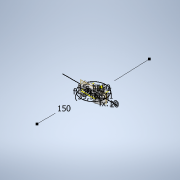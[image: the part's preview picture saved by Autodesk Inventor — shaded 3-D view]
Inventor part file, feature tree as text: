
AUTODESK INVENTOR PART (.ipt)
format: ipt  version: 2020.3 (Build 243373000, 373)  size: 541,184 bytes
history: native  units: mm
features: extrude x9, sketch x9, fillet x2, plane x1, loft x1, mirror x1
ambient origin geometry x8: Origin, YZ Plane, XZ Plane, XY Plane, X Axis, Y Axis, Z Axis, Center Point
bodies: Volumenkörper1 (feature_tree)
feature tree (23):
  extrude  "Extrusion1"  Depth=24.5mm
  extrude  "Extrusion2"  Depth=3.6mm
  extrude  "Extrusion3"  Depth=19.75mm
  extrude  "Extrusion4"  Depth=12.25mm
  sketch  "Skizze5"  dims[d8=0.0mm d9=4.0mm]
  extrude  "Extrusion5"  Depth=4.0mm
  extrude  "Extrusion7"  Depth=2.0mm
  extrude  "Extrusion8"  Depth=12.0mm
  extrude  "Extrusion6"  Depth=13.75mm
  plane  "Arbeitsebene1"
  extrude  "Extrusion9"  Depth=1.0mm TaperAngle=0.0deg
  loft  "Erhebung1"
  mirror  "Spiegeln1"
  fillet  "Rundung2"  Radius=2.0mm
  fillet  "Rundung3"  Radius=10.0mm
  sketch  "Skizze1"  dims[d0=31.5mm d1=24.5mm]
  sketch  "Skizze2"  dims[d2=4.5mm d3=3.6mm]
  sketch  "Skizze3"  dims[d4=39.5mm d5=19.75mm]
  sketch  "Skizze4"  dims[d6=15.75mm d7=12.25mm]
  sketch  "Skizze6"  dims[d10=37.0mm d11=0.0mm d13=2.0mm]
  sketch  "Skizze7"  dims[d14=10.0mm d15=0.0mm d16=12.0mm]
  sketch  "Skizze8"  dims[d17=20.0mm d18=13.75mm]
  sketch  "Skizze9"  dims[d19=39.5mm d20=5.0mm d21=0.0mm d22=2.0mm d23=2.0mm d24=10.0mm d25=0.0mm d26=3.6mm d27=2.0mm d28=8.0mm d29=5.826561mm d30=1.463907mm d31=68.0mm d32=20.0mm d33=10.0mm d34=5.5mm d35=5.5mm d36=29.0mm d37=14.5mm d38=150.0mm d39=150.0mm d40=11.0mm d41=11.0mm d42=39.5mm d43=19.75mm d44=15.0mm d45=10.0mm d46=0.0mm d47=10.0mm d48=0.0mm d49=10.0mm d50=0.0mm d51=10.0mm d52=0.0mm d53=5.0mm d54=37.0mm d55=18.5mm d56=4.0mm d57=15.0mm d58=0.0mm d59=10.0mm d60=16.0mm d61=13.5mm d62=0.0mm d63=90.0deg d64=0.0mm d65=90.0deg d66=1.0mm d67=1.0mm]
